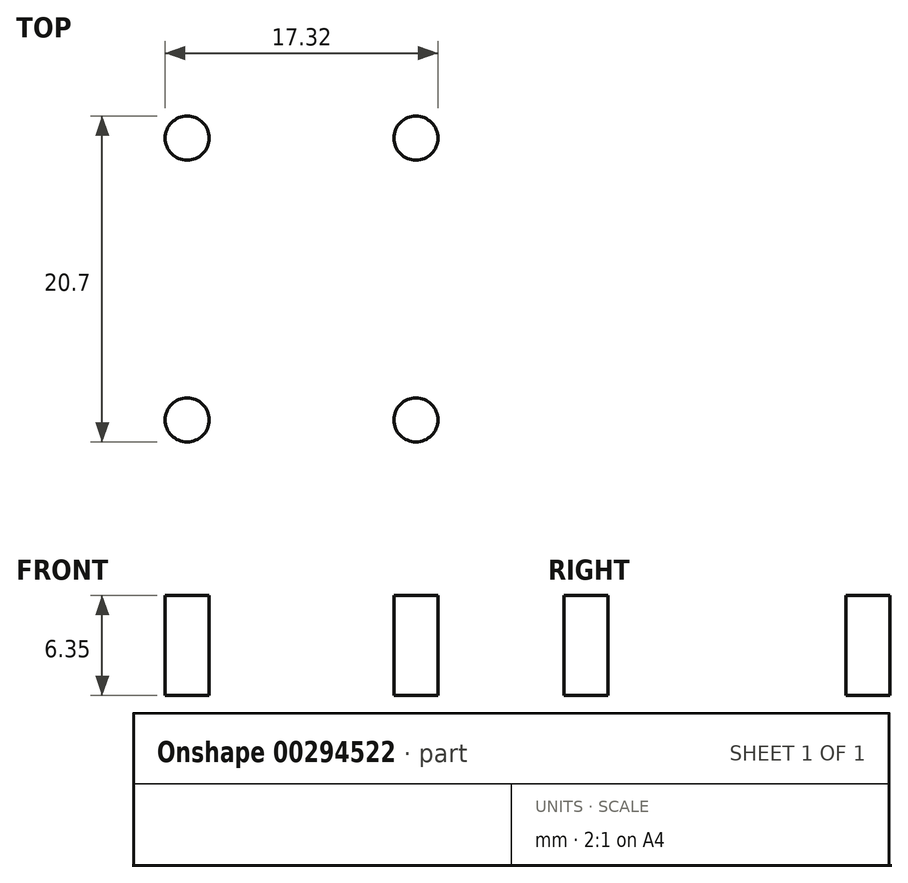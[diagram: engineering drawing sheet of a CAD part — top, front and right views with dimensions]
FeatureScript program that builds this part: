
annotation { "Feature Type Name" : "Feature", "Feature Type Description" : "" }
export const myFeature = defineFeature(function(context is Context, id is Id, definition is map)
    precondition{}
    {
        {
            var Q0;
            Q0=qCreatedBy(makeId("Top.planeOp"),FACE);
            var sketch = newSketch(context, id + "F0", { "sketchPlane" : qUnion([Q0])});
            skLineSegment(sketch, "E0.bottom", {"start": v(12.22, 11.68) * mm, "end": v(-12.22, 11.68) * mm});
            skLineSegment(sketch, "E0.top", {"start": v(12.22, -11.68) * mm, "end": v(-12.22, -11.68) * mm});
            skLineSegment(sketch, "E0.left", {"start": v(12.22, 11.68) * mm, "end": v(12.22, -11.68) * mm});
            skLineSegment(sketch, "E0.right", {"start": v(-12.22, 11.68) * mm, "end": v(-12.22, -11.68) * mm});
            skPoint(sketch, "E0.middle", {"position": v(0, 0) * mm});
            skLineSegment(sketch, "E1.bottom", {"start": v(4.76, 4.76) * mm, "end": v(-4.76, 4.76) * mm});
            skLineSegment(sketch, "E1.top", {"start": v(4.76, -4.76) * mm, "end": v(-4.76, -4.76) * mm});
            skLineSegment(sketch, "E1.left", {"start": v(4.76, 4.76) * mm, "end": v(4.76, -4.76) * mm});
            skLineSegment(sketch, "E1.right", {"start": v(-4.76, 4.76) * mm, "end": v(-4.76, -4.76) * mm});
            skSolve(sketch);
        }
        {
            var Q0;
            Q0=makeQuery(id+"F0.imprint","IMPRINT",FACE,{"disambiguationData":[TD([[makeQuery(id+"F0.imprint","IMPRINT",EDGE,{"derivedFrom":sQuery(id+"F0.wireOp",EDGE,"E0.bottom")}),1.0]])]});
            extrude(context, id + "F1", {"entities" : qUnion([Q0]), "depth" : 6.35 * mm});
        }
        {
            var Q0;
            Q0=makeQuery(id+"F1.opExtrude","CAP_FACE",FACE,{"disambiguationData":[OSD([sQuery(id+"F0.wireOp",EDGE,"E0.bottom"),sQuery(id+"F0.wireOp",EDGE,"E0.top"),sQuery(id+"F0.wireOp",EDGE,"E0.left"),sQuery(id+"F0.wireOp",EDGE,"E0.right"),sQuery(id+"F0.wireOp",EDGE,"E1.bottom"),sQuery(id+"F0.wireOp",EDGE,"E1.top"),sQuery(id+"F0.wireOp",EDGE,"E1.left"),sQuery(id+"F0.wireOp",EDGE,"E1.right")])],"isStart":false});
            var sketch = newSketch(context, id + "F2", { "sketchPlane" : qUnion([Q0])});
            skLineSegment(sketch, "E2", {"start": v(-12.22, 8.95) * mm, "end": v(12.22, 8.95) * mm});
            skLineSegment(sketch, "E3", {"start": v(-12.22, -8.95) * mm, "end": v(12.22, -8.95) * mm});
            skLineSegment(sketch, "E4", {"start": v(0, 11.68) * mm, "end": v(0, -11.68) * mm});
            skCircle(sketch, "E5", {"center": v(7.26, 8.95) * mm, "radius": 1.4 * mm});
            skCircle(sketch, "E6", {"center": v(7.26, -8.95) * mm, "radius": 1.4 * mm});
            skCircle(sketch, "E7.MirrorC", {"center": v(-7.26, 8.95) * mm, "radius": 1.4 * mm});
            skCircle(sketch, "E8.MirrorC", {"center": v(-7.26, -8.95) * mm, "radius": 1.4 * mm});
            skSolve(sketch);
        }
        {
            var Q0;
            Q0=makeQuery(id+"F1.opExtrude","SWEPT_EDGE",EDGE,{"disambiguationData":[OSD([sQuery(id+"F0.wireOp",EDGE,"E0.bottom"),sQuery(id+"F0.wireOp",EDGE,"E0.left")])]});
            var Q1;
            Q1=makeQuery(id+"F1.opExtrude","SWEPT_EDGE",EDGE,{"disambiguationData":[OSD([sQuery(id+"F0.wireOp",EDGE,"E0.bottom"),sQuery(id+"F0.wireOp",EDGE,"E0.right")])]});
            var Q2;
            Q2=makeQuery(id+"F1.opExtrude","SWEPT_EDGE",EDGE,{"disambiguationData":[OSD([sQuery(id+"F0.wireOp",EDGE,"E0.top"),sQuery(id+"F0.wireOp",EDGE,"E0.right")])]});
            var Q3;
            Q3=makeQuery(id+"F1.opExtrude","SWEPT_EDGE",EDGE,{"disambiguationData":[OSD([sQuery(id+"F0.wireOp",EDGE,"E0.top"),sQuery(id+"F0.wireOp",EDGE,"E0.left")])]});
            fillet(context, id + "F3", {"entities" : qUnion([Q0, Q1, Q2, Q3]), "radius" : 1.27 * mm, "tangentPropagation" : true, "allowEdgeOverflow" : false});
        }
        {
            var Q0;
            {var subQ0=sQuery(id+"F2.wireOp",EDGE,"E7.MirrorC");var subQ1=sQuery(id+"F2.wireOp",EDGE,"E2");var subQ2=makeQuery(id+"F2.imprint","INTERSECT",VERTEX,{"disambiguationData":[OD(0.0)],"derivedFrom":[subQ1,subQ0]});Q0=makeQuery(id+"F2.imprint","IMPRINT",FACE,{"disambiguationData":[TD([[makeQuery(id+"F2.imprint","IMPRINT",EDGE,{"disambiguationData":[TD([[subQ2,-1.0]])],"derivedFrom":subQ1}),1.0]])]});}
            var Q1;
            {var subQ0=sQuery(id+"F2.wireOp",EDGE,"E7.MirrorC");var subQ1=sQuery(id+"F2.wireOp",EDGE,"E2");var subQ2=makeQuery(id+"F2.imprint","INTERSECT",VERTEX,{"disambiguationData":[OD(0.0)],"derivedFrom":[subQ1,subQ0]});Q1=makeQuery(id+"F2.imprint","IMPRINT",FACE,{"disambiguationData":[TD([[makeQuery(id+"F2.imprint","IMPRINT",EDGE,{"disambiguationData":[TD([[subQ2,-1.0]])],"derivedFrom":subQ1}),-1.0]])]});}
            var Q2;
            {var subQ0=sQuery(id+"F2.wireOp",EDGE,"E5");var subQ1=sQuery(id+"F2.wireOp",EDGE,"E2");var subQ2=makeQuery(id+"F2.imprint","INTERSECT",VERTEX,{"disambiguationData":[OD(0.0)],"derivedFrom":[subQ1,subQ0]});Q2=makeQuery(id+"F2.imprint","IMPRINT",FACE,{"disambiguationData":[TD([[makeQuery(id+"F2.imprint","IMPRINT",EDGE,{"disambiguationData":[TD([[subQ2,-1.0]])],"derivedFrom":subQ1}),1.0]])]});}
            var Q3;
            {var subQ0=sQuery(id+"F2.wireOp",EDGE,"E5");var subQ1=sQuery(id+"F2.wireOp",EDGE,"E2");var subQ2=makeQuery(id+"F2.imprint","INTERSECT",VERTEX,{"disambiguationData":[OD(0.0)],"derivedFrom":[subQ1,subQ0]});Q3=makeQuery(id+"F2.imprint","IMPRINT",FACE,{"disambiguationData":[TD([[makeQuery(id+"F2.imprint","IMPRINT",EDGE,{"disambiguationData":[TD([[subQ2,-1.0]])],"derivedFrom":subQ1}),-1.0]])]});}
            var Q4;
            {var subQ0=sQuery(id+"F2.wireOp",EDGE,"E6");var subQ1=sQuery(id+"F2.wireOp",EDGE,"E3");var subQ2=makeQuery(id+"F2.imprint","INTERSECT",VERTEX,{"disambiguationData":[OD(0.0)],"derivedFrom":[subQ1,subQ0]});Q4=makeQuery(id+"F2.imprint","IMPRINT",FACE,{"disambiguationData":[TD([[makeQuery(id+"F2.imprint","IMPRINT",EDGE,{"disambiguationData":[TD([[subQ2,-1.0]])],"derivedFrom":subQ1}),1.0]])]});}
            var Q5;
            {var subQ0=sQuery(id+"F2.wireOp",EDGE,"E6");var subQ1=sQuery(id+"F2.wireOp",EDGE,"E3");var subQ2=makeQuery(id+"F2.imprint","INTERSECT",VERTEX,{"disambiguationData":[OD(0.0)],"derivedFrom":[subQ1,subQ0]});Q5=makeQuery(id+"F2.imprint","IMPRINT",FACE,{"disambiguationData":[TD([[makeQuery(id+"F2.imprint","IMPRINT",EDGE,{"disambiguationData":[TD([[subQ2,-1.0]])],"derivedFrom":subQ1}),-1.0]])]});}
            var Q6;
            {var subQ0=sQuery(id+"F2.wireOp",EDGE,"E8.MirrorC");var subQ1=sQuery(id+"F2.wireOp",EDGE,"E3");var subQ2=makeQuery(id+"F2.imprint","INTERSECT",VERTEX,{"disambiguationData":[OD(0.0)],"derivedFrom":[subQ1,subQ0]});Q6=makeQuery(id+"F2.imprint","IMPRINT",FACE,{"disambiguationData":[TD([[makeQuery(id+"F2.imprint","IMPRINT",EDGE,{"disambiguationData":[TD([[subQ2,-1.0]])],"derivedFrom":subQ1}),1.0]])]});}
            var Q7;
            {var subQ0=sQuery(id+"F2.wireOp",EDGE,"E8.MirrorC");var subQ1=sQuery(id+"F2.wireOp",EDGE,"E3");var subQ2=makeQuery(id+"F2.imprint","INTERSECT",VERTEX,{"disambiguationData":[OD(0.0)],"derivedFrom":[subQ1,subQ0]});Q7=makeQuery(id+"F2.imprint","IMPRINT",FACE,{"disambiguationData":[TD([[makeQuery(id+"F2.imprint","IMPRINT",EDGE,{"disambiguationData":[TD([[subQ2,-1.0]])],"derivedFrom":subQ1}),-1.0]])]});}
            extrude(context, id + "F4", {"entities" : qUnion([Q0, Q1, Q2, Q3, Q4, Q5, Q6, Q7]), "operationType" : NewBodyOperationType.REMOVE, "oppositeDirection" : true, "depth" : 6.35 * mm});
        }
    });
